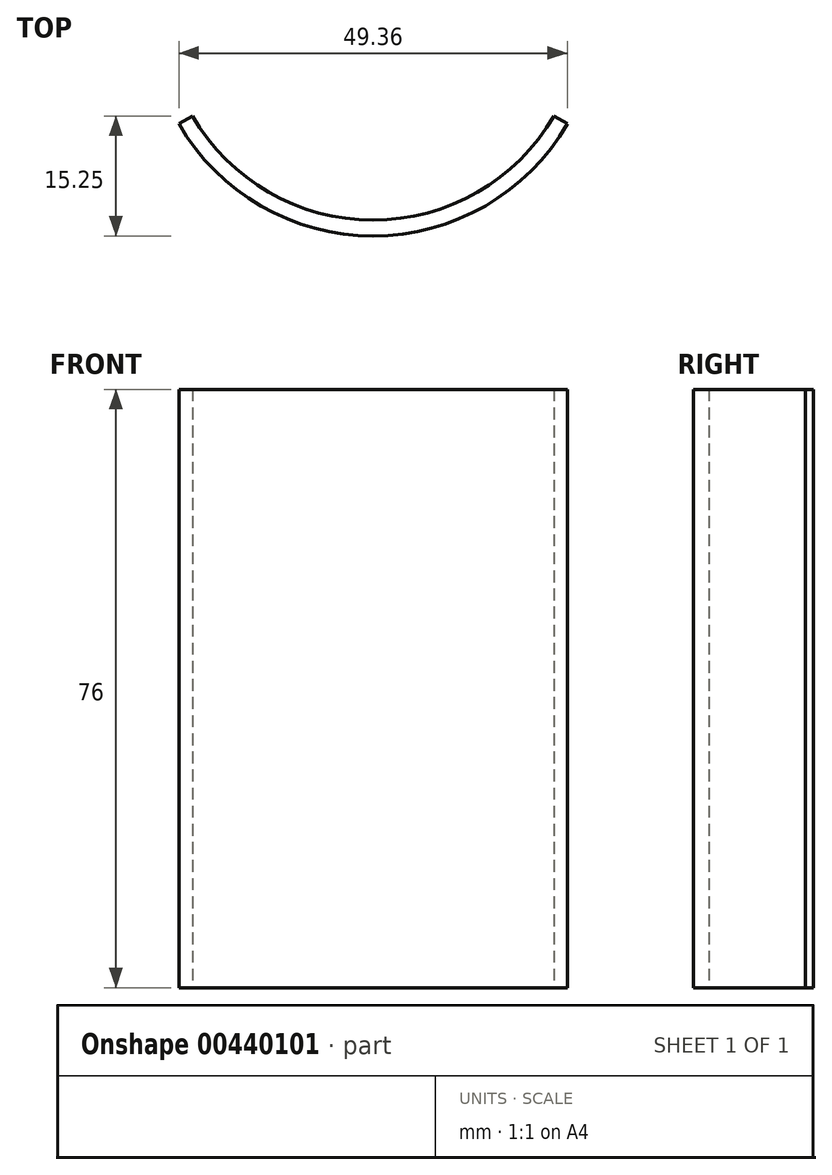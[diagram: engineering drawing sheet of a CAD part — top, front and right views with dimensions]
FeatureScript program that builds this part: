
annotation { "Feature Type Name" : "Feature", "Feature Type Description" : "" }
export const myFeature = defineFeature(function(context is Context, id is Id, definition is map)
    precondition{}
    {
        {
            var Q0;
            Q0=qCreatedBy(makeId("Top.planeOp"),FACE);
            var sketch = newSketch(context, id + "F0", { "sketchPlane" : qUnion([Q0])});
            skCircle(sketch, "E0", {"center": v(0, 0) * mm, "radius": 28.5 * mm});
            skCircle(sketch, "E1", {"center": v(0, 0) * mm, "radius": 26.5 * mm});
            skLineSegment(sketch, "E2", {"start": v(0, 0) * mm, "end": v(0, 28.5) * mm});
            skLineSegment(sketch, "E3", {"start": v(0, 0) * mm, "end": v(24.68, -14.25) * mm});
            skLineSegment(sketch, "E4", {"start": v(0, 0) * mm, "end": v(-24.68, -14.25) * mm});
            skSolve(sketch);
        }
        {
            var Q0;
            {var subQ0=sQuery(id+"F0.wireOp",EDGE,"E3");var subQ1=sQuery(id+"F0.wireOp",EDGE,"E0");var subQ2=makeQuery(id+"F0.imprint","INTERSECT",VERTEX,{"derivedFrom":[subQ1,subQ0]});Q0=makeQuery(id+"F0.imprint","IMPRINT",FACE,{"disambiguationData":[TD([[makeQuery(id+"F0.imprint","IMPRINT",EDGE,{"disambiguationData":[TD([[subQ2,1.0]])],"derivedFrom":subQ1}),1.0]])]});}
            extrude(context, id + "F1", {"entities" : qUnion([Q0]), "depth" : 76 * mm});
        }
    });
